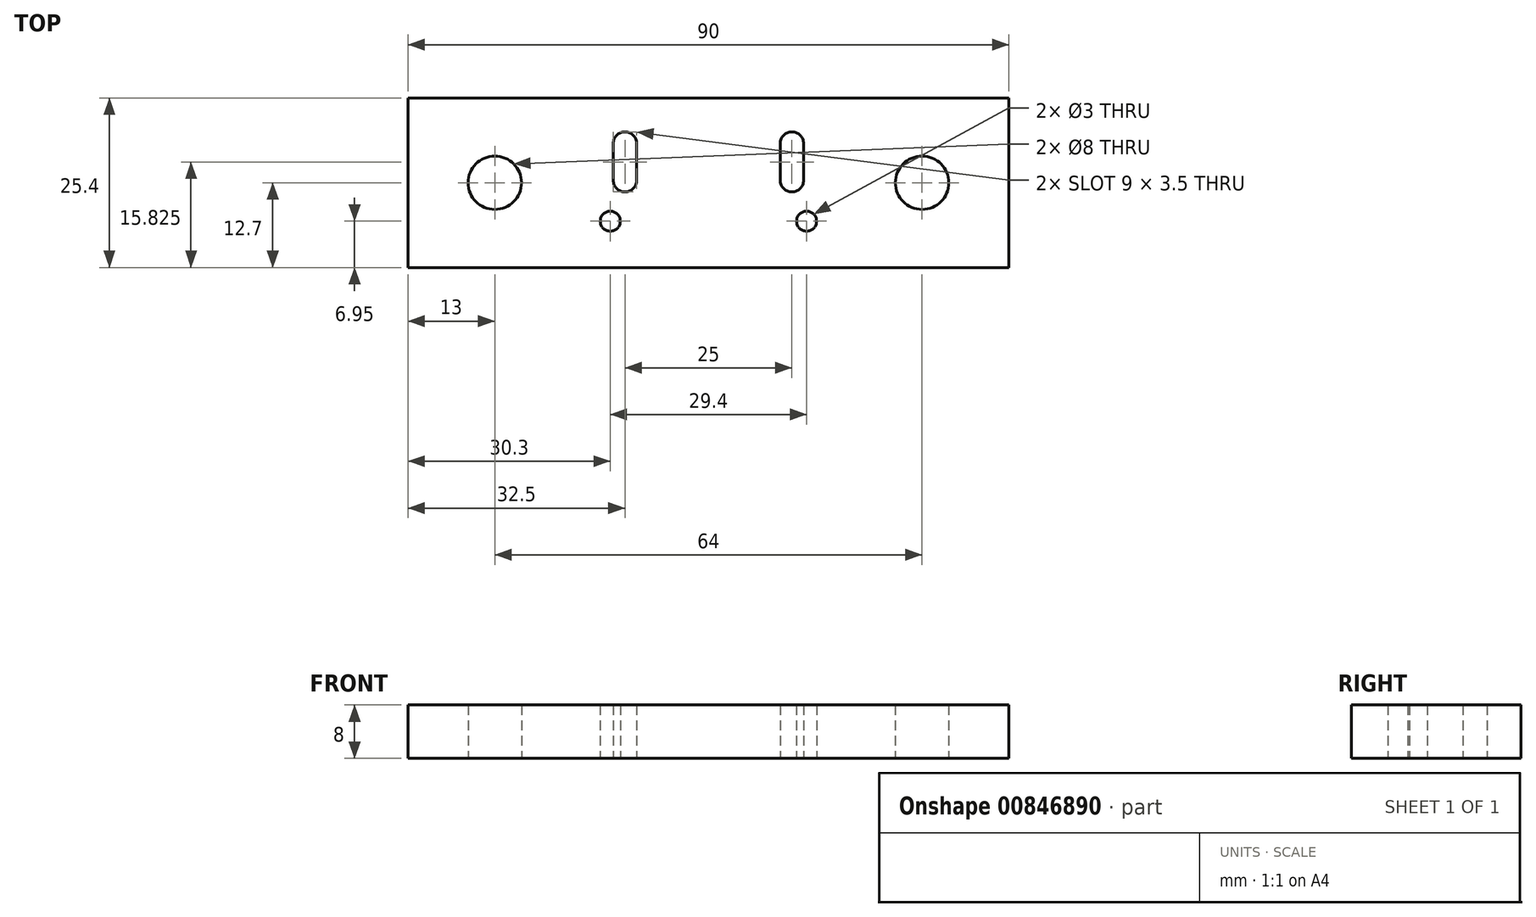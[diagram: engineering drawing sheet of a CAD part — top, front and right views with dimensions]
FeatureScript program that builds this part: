
annotation { "Feature Type Name" : "Feature", "Feature Type Description" : "" }
export const myFeature = defineFeature(function(context is Context, id is Id, definition is map)
    precondition{}
    {
        {
            var Q0;
            Q0=qCreatedBy(makeId("Top.planeOp"),FACE);
            var sketch = newSketch(context, id + "F0", { "sketchPlane" : qUnion([Q0])});
            skLineSegment(sketch, "E0", {"start": v(12.5, 0.37) * mm, "end": v(12.5, -5.12) * mm, "construction": true});
            skLineSegment(sketch, "E1", {"start": v(12.5, -5.12) * mm, "end": v(14.7, -5.12) * mm, "construction": true});
            skLineSegment(sketch, "E2", {"start": v(14.7, -5.12) * mm, "end": v(14.7, -11.25) * mm, "construction": true});
            skArc(sketch, "E3.0.startCap", {"start": v(10.75, 0.37) * mm, "mid": v(12.5, 2.12) * mm, "end": v(14.25, 0.37) * mm});
            skArc(sketch, "E3.0.endCap", {"start": v(14.25, -5.12) * mm, "mid": v(12.5, -6.88) * mm, "end": v(10.75, -5.12) * mm});
            skLineSegment(sketch, "E3.0.left", {"start": v(14.25, 0.37) * mm, "end": v(14.25, -5.12) * mm});
            skLineSegment(sketch, "E3.0.right", {"start": v(10.75, 0.37) * mm, "end": v(10.75, -5.12) * mm});
            skCircle(sketch, "E4", {"center": v(14.7, -11.25) * mm, "radius": 1.5 * mm});
            skArc(sketch, "E5.MirrorCS", {"start": v(-14.25, -5.12) * mm, "mid": v(-12.5, -6.88) * mm, "end": v(-10.75, -5.12) * mm});
            skLineSegment(sketch, "E6.MirrorCS", {"start": v(-10.75, 0.37) * mm, "end": v(-10.75, -5.12) * mm});
            skArc(sketch, "E7.MirrorCS", {"start": v(-10.75, 0.37) * mm, "mid": v(-12.5, 2.12) * mm, "end": v(-14.25, 0.37) * mm});
            skLineSegment(sketch, "E8.MirrorCS", {"start": v(-14.25, 0.37) * mm, "end": v(-14.25, -5.12) * mm});
            skCircle(sketch, "E9.MirrorC", {"center": v(-14.7, -11.25) * mm, "radius": 1.5 * mm});
            skPoint(sketch, "E10", {"position": v(0, -5.5) * mm});
            skLineSegment(sketch, "E11.bottom", {"start": v(-45, 7.2) * mm, "end": v(45, 7.2) * mm});
            skLineSegment(sketch, "E11.top", {"start": v(-45, -18.2) * mm, "end": v(45, -18.2) * mm});
            skLineSegment(sketch, "E11.left", {"start": v(-45, 7.2) * mm, "end": v(-45, -18.2) * mm});
            skLineSegment(sketch, "E11.right", {"start": v(45, 7.2) * mm, "end": v(45, -18.2) * mm});
            skLineSegment(sketch, "E12", {"start": v(0, -5.5) * mm, "end": v(0, -18.2) * mm, "construction": true});
            skLineSegment(sketch, "E13", {"start": v(-45, -5.5) * mm, "end": v(-32, -5.5) * mm, "construction": true});
            skCircle(sketch, "E14", {"center": v(-32, -5.5) * mm, "radius": 4 * mm});
            skCircle(sketch, "E15.MirrorC", {"center": v(32, -5.5) * mm, "radius": 4 * mm});
            skSolve(sketch);
        }
        {
            var Q0;
            Q0 = qSketchRegion(id + "F0", true);
            extrude(context, id + "F1", {"entities" : qUnion([Q0]), "depth" : 8 * mm, "offsetDistance" : 25 * mm});
        }
    });
